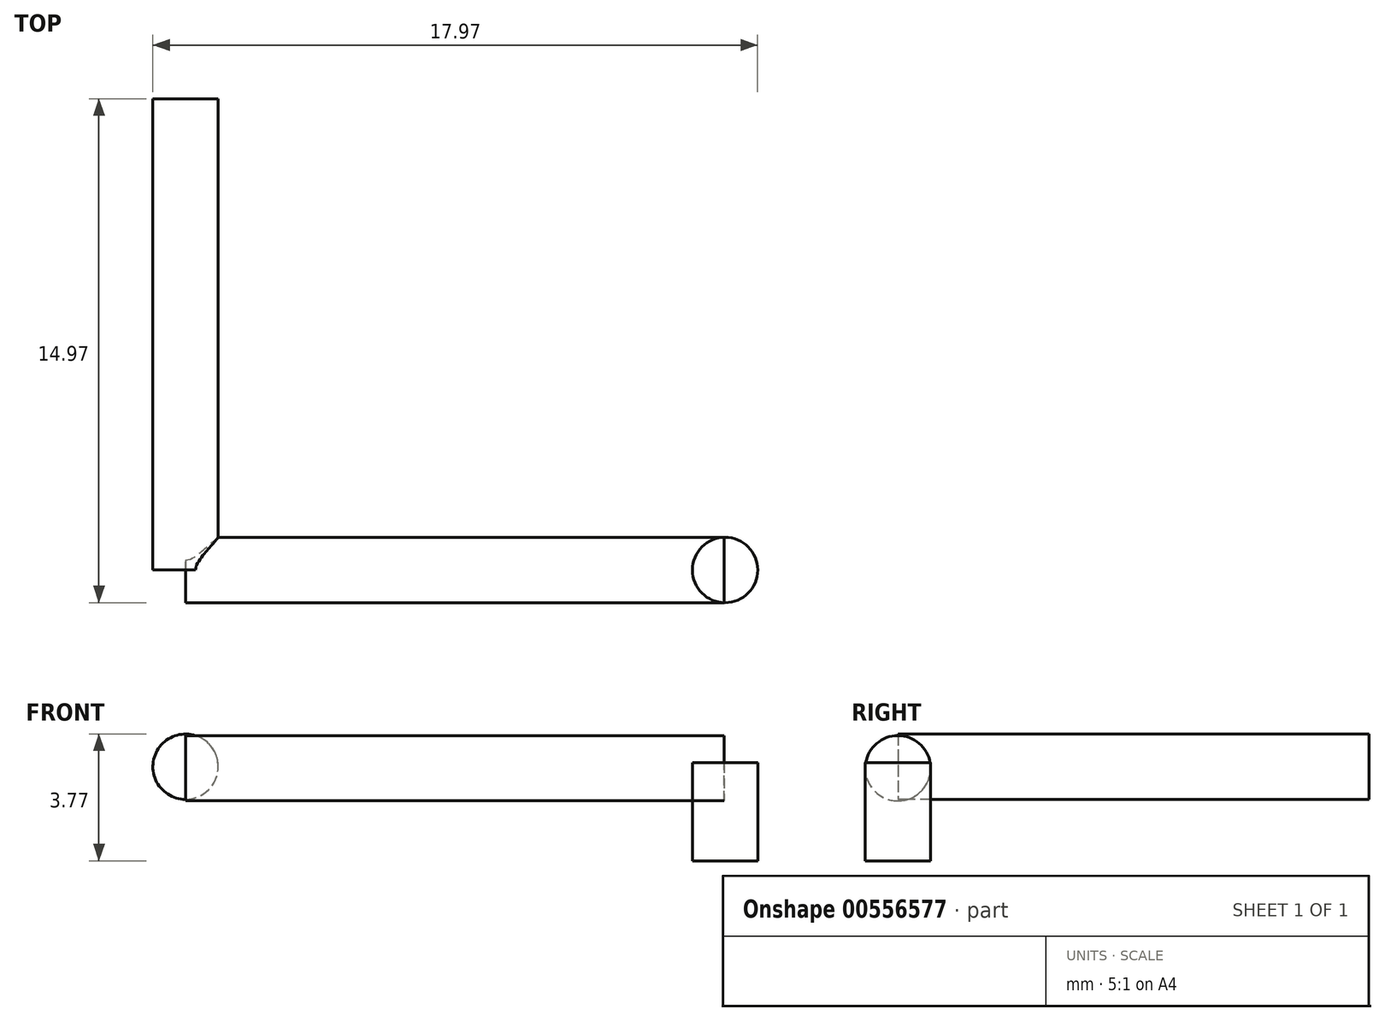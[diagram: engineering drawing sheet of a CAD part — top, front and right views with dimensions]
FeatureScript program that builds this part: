
annotation { "Feature Type Name" : "Feature", "Feature Type Description" : "" }
export const myFeature = defineFeature(function(context is Context, id is Id, definition is map)
    precondition{}
    {
        {
            var Q0;
            Q0=qCreatedBy(makeId("Right.planeOp"),FACE);
            var sketch = newSketch(context, id + "F0", { "sketchPlane" : qUnion([Q0])});
            skCircle(sketch, "E0", {"center": v(0, 1.94) * mm, "radius": 0.97 * mm});
            skSolve(sketch);
        }
        {
            var Q0;
            Q0=makeQuery(id+"F0.imprint","IMPRINT",FACE,{"disambiguationData":[TD([[makeQuery(id+"F0.imprint","IMPRINT",EDGE,{"derivedFrom":sQuery(id+"F0.wireOp",EDGE,"E0")}),1.0]])]});
            extrude(context, id + "F1", {"entities" : qUnion([Q0]), "depth" : 16 * mm, "offsetDistance" : 25 * mm});
        }
        {
            var Q0;
            Q0=qCreatedBy(makeId("Front.planeOp"),FACE);
            var sketch = newSketch(context, id + "F2", { "sketchPlane" : qUnion([Q0])});
            skCircle(sketch, "E1", {"center": v(0, 1.99) * mm, "radius": 0.97 * mm});
            skSolve(sketch);
        }
        {
            var Q0;
            Q0 = qSketchRegion(id + "F2", true);
            extrude(context, id + "F3", {"entities" : qUnion([Q0]), "operationType" : NewBodyOperationType.ADD, "depth" : -14 * mm, "offsetDistance" : 25 * mm});
        }
        {
            var Q0;
            Q0=qCreatedBy(makeId("Top.planeOp"),FACE);
            var sketch = newSketch(context, id + "F4", { "sketchPlane" : qUnion([Q0])});
            skCircle(sketch, "E2", {"center": v(14.02, 0) * mm, "radius": 0.97 * mm});
            skSolve(sketch);
        }
        {
            var Q0;
            Q0=makeQuery(id+"F4.imprint","IMPRINT",FACE,{"disambiguationData":[TD([[makeQuery(id+"F4.imprint","IMPRINT",EDGE,{"derivedFrom":sQuery(id+"F4.wireOp",EDGE,"E2")}),1.0]])]});
            extrude(context, id + "F5", {"entities" : qUnion([Q0]), "depth" : -2.91 * mm, "offsetDistance" : 25 * mm});
        }
        {
            var Q0;
            Q0=makeQuery(id+"F5.opExtrude","SWEPT_BODY",BODY,{"disambiguationData":[OSD([sQuery(id+"F4.wireOp",EDGE,"E2")])]});
            transform(context, id + "F6", {"entities" : qUnion([Q0]), "transformType" : TransformType.TRANSLATION_3D, "dx" : 2 * mm, "dy" : 0 * mm, "dz" : 2.1 * mm, "makeCopy" : false});
        }
    });
